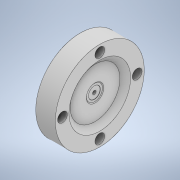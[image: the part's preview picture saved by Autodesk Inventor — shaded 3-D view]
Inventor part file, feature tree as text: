
AUTODESK INVENTOR PART (.ipt)
format: ipt  version: 2020 (Build 240168000, 168)  size: 158,720 bytes
history: native  units: mm
features: other x3, revolve x1, sketch x1
ambient origin geometry x8: Origin, YZ Plane, XZ Plane, XY Plane, X Axis, Y Axis, Z Axis, Center Point
bodies: Solid1 (feature_tree)
feature tree (5):
  other  "malv2.ipt"
  revolve  "Revolution1"  Angle=90.0deg
  other  "Solid1::malv2.ipt"
  other  "TaggingFeature2"
  sketch  "Sketch1"  dims[d0=10.0mm d1=90.0deg d2=0.872665mm d3=0.5mm d4=0.872665mm]
